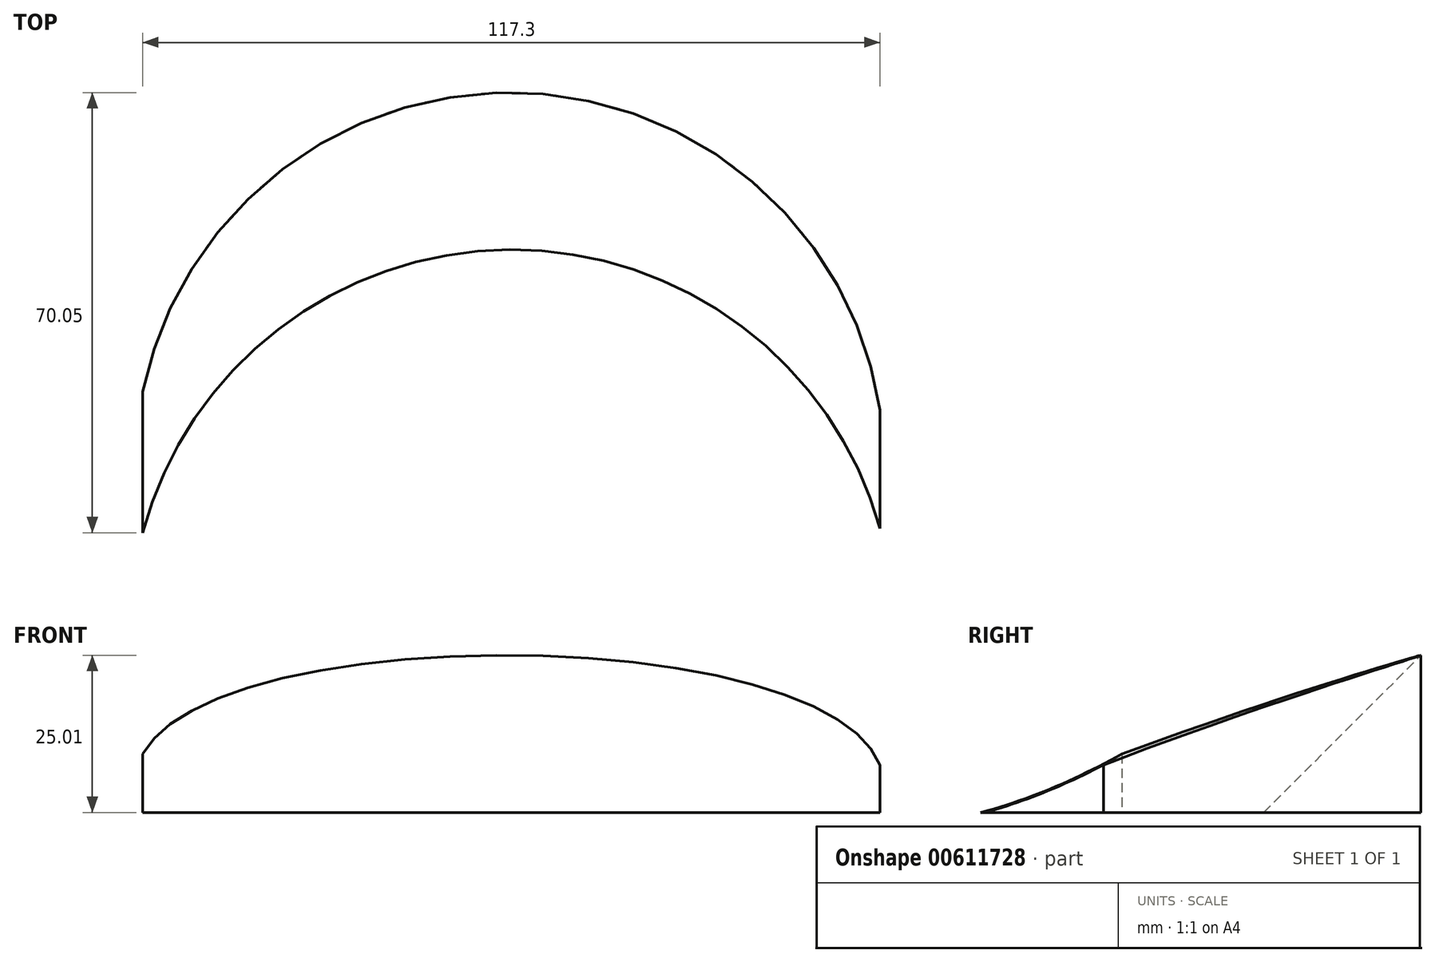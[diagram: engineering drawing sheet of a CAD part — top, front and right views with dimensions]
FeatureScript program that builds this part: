
annotation { "Feature Type Name" : "Feature", "Feature Type Description" : "" }
export const myFeature = defineFeature(function(context is Context, id is Id, definition is map)
    precondition{}
    {
        {
            var Q0;
            Q0=qCreatedBy(makeId("Top.planeOp"),FACE);
            var sketch = newSketch(context, id + "F0", { "sketchPlane" : qUnion([Q0])});
            skLineSegment(sketch, "E0.bottom", {"start": v(0, 0) * mm, "end": v(-206.97, 0) * mm});
            skLineSegment(sketch, "E0.top", {"start": v(0, 93.9) * mm, "end": v(-206.97, 93.9) * mm});
            skLineSegment(sketch, "E0.left", {"start": v(0, 0) * mm, "end": v(0, 93.9) * mm});
            skLineSegment(sketch, "E0.right", {"start": v(-206.97, 0) * mm, "end": v(-206.97, 93.9) * mm});
            skSolve(sketch);
        }
        {
            var Q0;
            Q0=makeQuery(id+"F0.imprint","IMPRINT",FACE,{"disambiguationData":[TD([[makeQuery(id+"F0.imprint","IMPRINT",EDGE,{"derivedFrom":sQuery(id+"F0.wireOp",EDGE,"E0.bottom")}),-1.0]])]});
            extrude(context, id + "F1", {"entities" : qUnion([Q0]), "depth" : 38.1 * mm, "offsetDistance" : 25.4 * mm});
        }
        {
            var Q0;
            Q0=makeQuery(id+"F1.opExtrude","CAP_FACE",FACE,{"disambiguationData":[OSD([sQuery(id+"F0.wireOp",EDGE,"E0.bottom"),sQuery(id+"F0.wireOp",EDGE,"E0.top"),sQuery(id+"F0.wireOp",EDGE,"E0.left"),sQuery(id+"F0.wireOp",EDGE,"E0.right")])],"isStart":false});
            var sketch = newSketch(context, id + "F2", { "sketchPlane" : qUnion([Q0])});
            skArc(sketch, "E1", {"start": v(-38.55, 38.1) * mm, "mid": v(-95.96, 88.6) * mm, "end": v(-155.85, 41.06) * mm});
            skLineSegment(sketch, "E2", {"start": v(-155.85, 41.06) * mm, "end": v(-155.85, 18.57) * mm});
            skLineSegment(sketch, "E3", {"start": v(-38.55, 38.1) * mm, "end": v(-38.55, 19.27) * mm});
            skArc(sketch, "E4", {"start": v(-38.55, 19.27) * mm, "mid": v(-97.47, 63.6) * mm, "end": v(-155.85, 18.57) * mm});
            skArc(sketch, "E5", {"start": v(-38.55, 19.27) * mm, "mid": v(-97.55, 77.92) * mm, "end": v(-155.85, 18.57) * mm});
            skSolve(sketch);
        }
        {
            var Q0;
            Q0=makeQuery(id+"F2.imprint","IMPRINT",FACE,{"disambiguationData":[TD([[makeQuery(id+"F2.imprint","IMPRINT",EDGE,{"derivedFrom":sQuery(id+"F2.wireOp",EDGE,"E1")}),1.0]])]});
            extrude(context, id + "F3", {"entities" : qUnion([Q0]), "operationType" : NewBodyOperationType.ADD, "depth" : 38.1 * mm, "offsetDistance" : 25.4 * mm});
        }
        {
            var Q0;
            {var subQ1=sQuery(id+"F2.wireOp",EDGE,"E4");Q0=makeQuery(id+"F2.imprint","IMPRINT",FACE,{"disambiguationData":[TD([[makeQuery(id+"F2.imprint","IMPRINT",EDGE,{"derivedFrom":subQ1}),-1.0]])]});}
            extrude(context, id + "F4", {"entities" : qUnion([Q0]), "operationType" : NewBodyOperationType.ADD, "depth" : 38.1 * mm, "offsetDistance" : 25.4 * mm});
        }
        {
            var Q0;
            Q0=makeQuery(id+"F4.opExtrude","CAP_EDGE",EDGE,{"disambiguationData":[OSD([sQuery(id+"F2.wireOp",EDGE,"E4")])],"isStart":false});
            chamfer(context, id + "F5", {"entities" : qUnion([Q0]), "width" : 38.1 * mm, "tangentPropagation" : true});
        }
        {
            var Q0;
            Q0=makeQuery(id+"F1.opExtrude","SWEPT_FACE",FACE,{"disambiguationData":[OSD([sQuery(id+"F0.wireOp",EDGE,"E0.bottom")])]});
            var sketch = newSketch(context, id + "F6", { "sketchPlane" : qUnion([Q0])});
            skLineSegment(sketch, "E6.bottom", {"start": v(0, 38.1) * mm, "end": v(-206.97, 38.1) * mm});
            skLineSegment(sketch, "E6.top", {"start": v(0, 0) * mm, "end": v(-206.97, 0) * mm});
            skLineSegment(sketch, "E6.left", {"start": v(0, 38.1) * mm, "end": v(0, 0) * mm});
            skLineSegment(sketch, "E6.right", {"start": v(-206.97, 38.1) * mm, "end": v(-206.97, 0) * mm});
            skSolve(sketch);
        }
        {
            var Q0;
            Q0=makeQuery(id+"F6.imprint","IMPRINT",FACE,{"disambiguationData":[TD([[makeQuery(id+"F6.imprint","IMPRINT",EDGE,{"derivedFrom":sQuery(id+"F6.wireOp",EDGE,"E6.bottom")}),1.0]])]});
            var sketch = newSketch(context, id + "F7", { "sketchPlane" : qUnion([Q0])});
            skSolve(sketch);
        }
        {
            var Q0;
            Q0 = qSketchRegion(id + "F7", true);
            var Q1;
            Q1=makeQuery(id+"F6.imprint","IMPRINT",FACE,{"disambiguationData":[TD([[makeQuery(id+"F6.imprint","IMPRINT",EDGE,{"derivedFrom":sQuery(id+"F6.wireOp",EDGE,"E6.bottom")}),1.0]])]});
            extrude(context, id + "F8", {"entities" : qUnion([Q0, Q1]), "operationType" : NewBodyOperationType.REMOVE, "oppositeDirection" : true, "depth" : 152.4 * mm, "offsetDistance" : 25.4 * mm});
        }
    });
